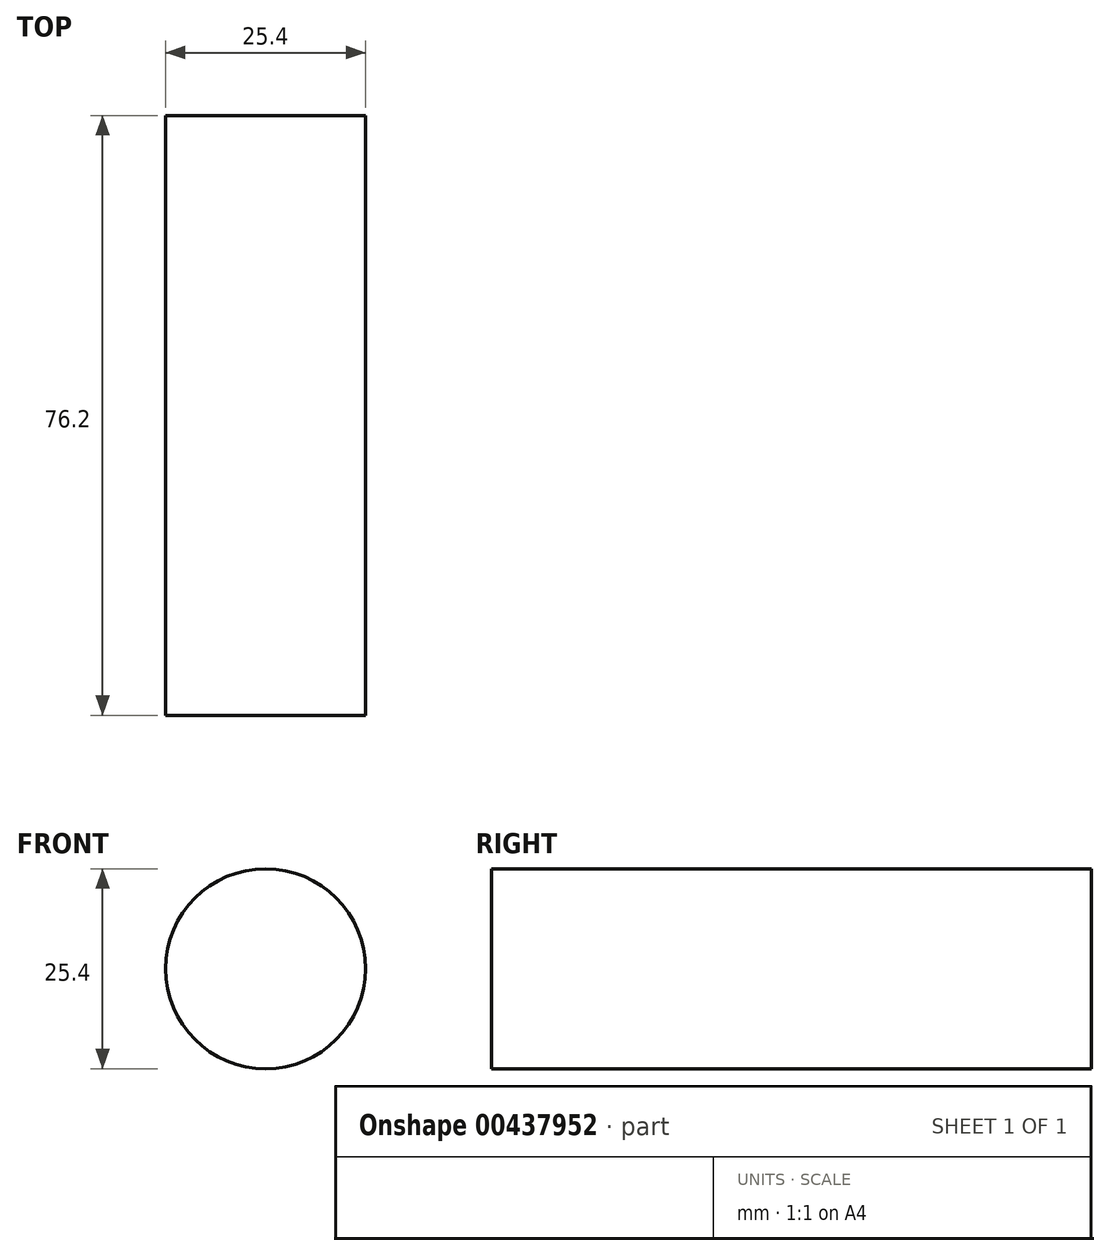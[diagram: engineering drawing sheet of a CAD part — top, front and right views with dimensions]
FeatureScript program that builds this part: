
annotation { "Feature Type Name" : "Feature", "Feature Type Description" : "" }
export const myFeature = defineFeature(function(context is Context, id is Id, definition is map)
    precondition{}
    {
        {
            var Q0;
            Q0=qCreatedBy(makeId("Front.planeOp"),FACE);
            var sketch = newSketch(context, id + "F0", { "sketchPlane" : qUnion([Q0])});
            skCircle(sketch, "E0", {"center": v(-27.3, 17.19) * mm, "radius": 12.7 * mm});
            skSolve(sketch);
        }
        {
            var Q0;
            Q0=makeQuery(id+"F0.imprint","IMPRINT",FACE,{"disambiguationData":[TD([[makeQuery(id+"F0.imprint","IMPRINT",EDGE,{"derivedFrom":sQuery(id+"F0.wireOp",EDGE,"E0")}),1.0]])]});
            extrude(context, id + "F1", {"entities" : qUnion([Q0]), "depth" : 76.2 * mm});
        }
    });
